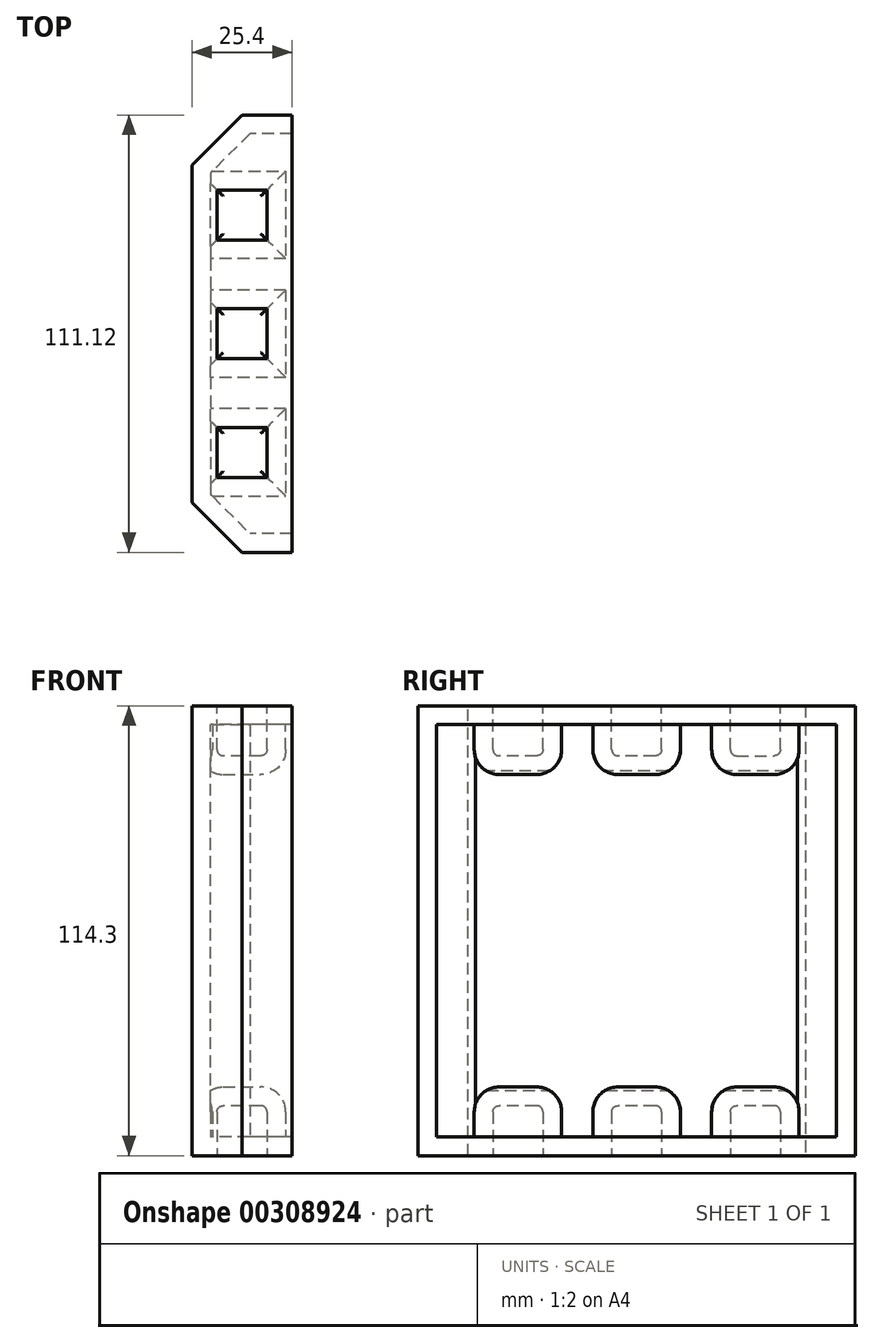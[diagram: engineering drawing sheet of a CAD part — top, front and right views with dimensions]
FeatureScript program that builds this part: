
annotation { "Feature Type Name" : "Feature", "Feature Type Description" : "" }
export const myFeature = defineFeature(function(context is Context, id is Id, definition is map)
    precondition{}
    {
        {
            var Q0;
            Q0=qCreatedBy(makeId("Right.planeOp"),FACE);
            var sketch = newSketch(context, id + "F0", { "sketchPlane" : qUnion([Q0])});
            skLineSegment(sketch, "E0.bottom", {"start": v(55.56, -57.15) * mm, "end": v(-55.56, -57.15) * mm});
            skLineSegment(sketch, "E0.top", {"start": v(55.56, 57.15) * mm, "end": v(-55.56, 57.15) * mm});
            skLineSegment(sketch, "E0.left", {"start": v(55.56, -57.15) * mm, "end": v(55.56, 57.15) * mm});
            skLineSegment(sketch, "E0.right", {"start": v(-55.56, -57.15) * mm, "end": v(-55.56, 57.15) * mm});
            skPoint(sketch, "E0.middle", {"position": v(0, 0) * mm});
            skSolve(sketch);
        }
        {
            var Q0;
            Q0 = qSketchRegion(id + "F0", true);
            extrude(context, id + "F1", {"entities" : qUnion([Q0]), "depth" : 25.4 * mm});
        }
        {
            var Q0;
            Q0=makeQuery(id+"F1.opExtrude","CAP_EDGE",EDGE,{"disambiguationData":[OSD([sQuery(id+"F0.wireOp",EDGE,"E0.right")])],"isStart":true});
            var Q1;
            Q1=makeQuery(id+"F1.opExtrude","CAP_EDGE",EDGE,{"disambiguationData":[OSD([sQuery(id+"F0.wireOp",EDGE,"E0.left")])],"isStart":true});
            chamfer(context, id + "F2", {"entities" : qUnion([Q0, Q1]), "width" : 12.7 * mm, "tangentPropagation" : true});
        }
        {
            var Q0;
            Q0=makeQuery(id+"F1.opExtrude","SWEPT_FACE",FACE,{"disambiguationData":[OSD([sQuery(id+"F0.wireOp",EDGE,"E0.top")])]});
            var sketch = newSketch(context, id + "F3", { "sketchPlane" : qUnion([Q0])});
            skLineSegment(sketch, "E1.bottom", {"start": v(19.05, 23.81) * mm, "end": v(6.35, 23.81) * mm});
            skLineSegment(sketch, "E1.top", {"start": v(19.05, 36.51) * mm, "end": v(6.35, 36.51) * mm});
            skLineSegment(sketch, "E1.left", {"start": v(19.05, 23.81) * mm, "end": v(19.05, 36.51) * mm});
            skLineSegment(sketch, "E1.right", {"start": v(6.35, 23.81) * mm, "end": v(6.35, 36.51) * mm});
            skPoint(sketch, "E1.middle", {"position": v(12.7, 30.16) * mm});
            skPoint(sketch, "E1.cornerSnap0", {"position": v(19.05, 55.56) * mm});
            skLineSegment(sketch, "E2.bottom", {"start": v(19.05, -23.81) * mm, "end": v(6.35, -23.81) * mm});
            skLineSegment(sketch, "E2.top", {"start": v(19.05, -36.51) * mm, "end": v(6.35, -36.51) * mm});
            skLineSegment(sketch, "E2.left", {"start": v(19.05, -23.81) * mm, "end": v(19.05, -36.51) * mm});
            skLineSegment(sketch, "E2.right", {"start": v(6.35, -23.81) * mm, "end": v(6.35, -36.51) * mm});
            skPoint(sketch, "E2.middle", {"position": v(12.7, -30.16) * mm});
            skPoint(sketch, "E2.cornerSnap0", {"position": v(19.05, -55.56) * mm});
            skLineSegment(sketch, "E3.bottom", {"start": v(19.05, 6.35) * mm, "end": v(6.35, 6.35) * mm});
            skLineSegment(sketch, "E3.top", {"start": v(19.05, -6.35) * mm, "end": v(6.35, -6.35) * mm});
            skLineSegment(sketch, "E3.left", {"start": v(19.05, 6.35) * mm, "end": v(19.05, -6.35) * mm});
            skLineSegment(sketch, "E3.right", {"start": v(6.35, 6.35) * mm, "end": v(6.35, -6.35) * mm});
            skPoint(sketch, "E3.middle", {"position": v(12.7, 0) * mm});
            skSolve(sketch);
        }
        {
            var Q0;
            Q0 = qSketchRegion(id + "F3", true);
            extrude(context, id + "F4", {"entities" : qUnion([Q0]), "operationType" : NewBodyOperationType.REMOVE, "oppositeDirection" : true, "depth" : 12.7 * mm});
        }
        {
            var Q0;
            Q0=makeQuery(id+"F4.boolean.opBoolean","COPY",FACE,{"derivedFrom":makeQuery(id+"F4.opExtrude","CAP_FACE",FACE,{"disambiguationData":[OSD([sQuery(id+"F3.wireOp",EDGE,"E1.bottom"),sQuery(id+"F3.wireOp",EDGE,"E1.top"),sQuery(id+"F3.wireOp",EDGE,"E1.left"),sQuery(id+"F3.wireOp",EDGE,"E1.right")])],"isStart":false})});
            var Q1;
            Q1=makeQuery(id+"F4.boolean.opBoolean","COPY",FACE,{"derivedFrom":makeQuery(id+"F4.opExtrude","CAP_FACE",FACE,{"disambiguationData":[OSD([sQuery(id+"F3.wireOp",EDGE,"E3.bottom"),sQuery(id+"F3.wireOp",EDGE,"E3.top"),sQuery(id+"F3.wireOp",EDGE,"E3.left"),sQuery(id+"F3.wireOp",EDGE,"E3.right")])],"isStart":false})});
            var Q2;
            Q2=makeQuery(id+"F4.boolean.opBoolean","COPY",FACE,{"derivedFrom":makeQuery(id+"F4.opExtrude","CAP_FACE",FACE,{"disambiguationData":[OSD([sQuery(id+"F3.wireOp",EDGE,"E2.bottom"),sQuery(id+"F3.wireOp",EDGE,"E2.top"),sQuery(id+"F3.wireOp",EDGE,"E2.left"),sQuery(id+"F3.wireOp",EDGE,"E2.right")])],"isStart":false})});
            fillet(context, id + "F5", {"entities" : qUnion([Q0, Q1, Q2]), "radius" : 1.59 * mm, "tangentPropagation" : true, "allowEdgeOverflow" : false});
        }
        {
            var Q0;
            Q0=makeQuery(id+"F1.opExtrude","SWEPT_FACE",FACE,{"disambiguationData":[OSD([sQuery(id+"F0.wireOp",EDGE,"E0.bottom")])]});
            var sketch = newSketch(context, id + "F6", { "sketchPlane" : qUnion([Q0])});
            skLineSegment(sketch, "E4.bottom", {"start": v(19.05, 23.81) * mm, "end": v(6.35, 23.81) * mm});
            skLineSegment(sketch, "E4.top", {"start": v(19.05, 36.51) * mm, "end": v(6.35, 36.51) * mm});
            skLineSegment(sketch, "E4.left", {"start": v(19.05, 23.81) * mm, "end": v(19.05, 36.51) * mm});
            skLineSegment(sketch, "E4.right", {"start": v(6.35, 23.81) * mm, "end": v(6.35, 36.51) * mm});
            skPoint(sketch, "E4.middle", {"position": v(12.7, 30.16) * mm});
            skPoint(sketch, "E4.cornerSnap0", {"position": v(19.05, 55.56) * mm});
            skLineSegment(sketch, "E5.bottom", {"start": v(19.05, -36.51) * mm, "end": v(6.35, -36.51) * mm});
            skLineSegment(sketch, "E5.top", {"start": v(19.05, -23.81) * mm, "end": v(6.35, -23.81) * mm});
            skLineSegment(sketch, "E5.left", {"start": v(19.05, -36.51) * mm, "end": v(19.05, -23.81) * mm});
            skLineSegment(sketch, "E5.right", {"start": v(6.35, -36.51) * mm, "end": v(6.35, -23.81) * mm});
            skPoint(sketch, "E5.middle", {"position": v(12.7, -30.16) * mm});
            skPoint(sketch, "E5.cornerSnap0", {"position": v(19.05, -55.56) * mm});
            skLineSegment(sketch, "E6.bottom", {"start": v(19.05, -6.35) * mm, "end": v(6.35, -6.35) * mm});
            skLineSegment(sketch, "E6.top", {"start": v(19.05, 6.35) * mm, "end": v(6.35, 6.35) * mm});
            skLineSegment(sketch, "E6.left", {"start": v(19.05, -6.35) * mm, "end": v(19.05, 6.35) * mm});
            skLineSegment(sketch, "E6.right", {"start": v(6.35, -6.35) * mm, "end": v(6.35, 6.35) * mm});
            skPoint(sketch, "E6.middle", {"position": v(12.7, 0) * mm});
            skPoint(sketch, "E6.middle.positionSnap0", {"position": v(12.7, 23.81) * mm});
            skPoint(sketch, "E6.middle.positionSnap1", {"position": v(25.4, 0) * mm});
            skPoint(sketch, "E6.centerSnap0", {"position": v(12.7, 23.81) * mm});
            skPoint(sketch, "E6.centerSnap1", {"position": v(25.4, 0) * mm});
            skSolve(sketch);
        }
        {
            var Q0;
            Q0 = qSketchRegion(id + "F6", true);
            extrude(context, id + "F7", {"entities" : qUnion([Q0]), "operationType" : NewBodyOperationType.REMOVE, "oppositeDirection" : true, "depth" : 12.7 * mm});
        }
        {
            var Q0;
            Q0=makeQuery(id+"F7.boolean.opBoolean","COPY",FACE,{"derivedFrom":makeQuery(id+"F7.opExtrude","CAP_FACE",FACE,{"disambiguationData":[OSD([sQuery(id+"F6.wireOp",EDGE,"E4.bottom"),sQuery(id+"F6.wireOp",EDGE,"E4.top"),sQuery(id+"F6.wireOp",EDGE,"E4.left"),sQuery(id+"F6.wireOp",EDGE,"E4.right")])],"isStart":false})});
            var Q1;
            Q1=makeQuery(id+"F7.boolean.opBoolean","COPY",FACE,{"derivedFrom":makeQuery(id+"F7.opExtrude","CAP_FACE",FACE,{"disambiguationData":[OSD([sQuery(id+"F6.wireOp",EDGE,"E6.bottom"),sQuery(id+"F6.wireOp",EDGE,"E6.top"),sQuery(id+"F6.wireOp",EDGE,"E6.left"),sQuery(id+"F6.wireOp",EDGE,"E6.right")])],"isStart":false})});
            var Q2;
            Q2=makeQuery(id+"F7.boolean.opBoolean","COPY",FACE,{"derivedFrom":makeQuery(id+"F7.opExtrude","CAP_FACE",FACE,{"disambiguationData":[OSD([sQuery(id+"F6.wireOp",EDGE,"E5.bottom"),sQuery(id+"F6.wireOp",EDGE,"E5.top"),sQuery(id+"F6.wireOp",EDGE,"E5.left"),sQuery(id+"F6.wireOp",EDGE,"E5.right")])],"isStart":false})});
            fillet(context, id + "F8", {"entities" : qUnion([Q0, Q1, Q2]), "radius" : 1.59 * mm, "tangentPropagation" : true, "allowEdgeOverflow" : false});
        }
        {
            var Q0;
            Q0=makeQuery(id+"F1.opExtrude","CAP_FACE",FACE,{"disambiguationData":[OSD([sQuery(id+"F0.wireOp",EDGE,"E0.bottom"),sQuery(id+"F0.wireOp",EDGE,"E0.top"),sQuery(id+"F0.wireOp",EDGE,"E0.left"),sQuery(id+"F0.wireOp",EDGE,"E0.right")])],"isStart":false});
            shell(context, id + "F9", {"entities" : qUnion([Q0]), "thickness" : 4.76 * mm});
        }
    });
